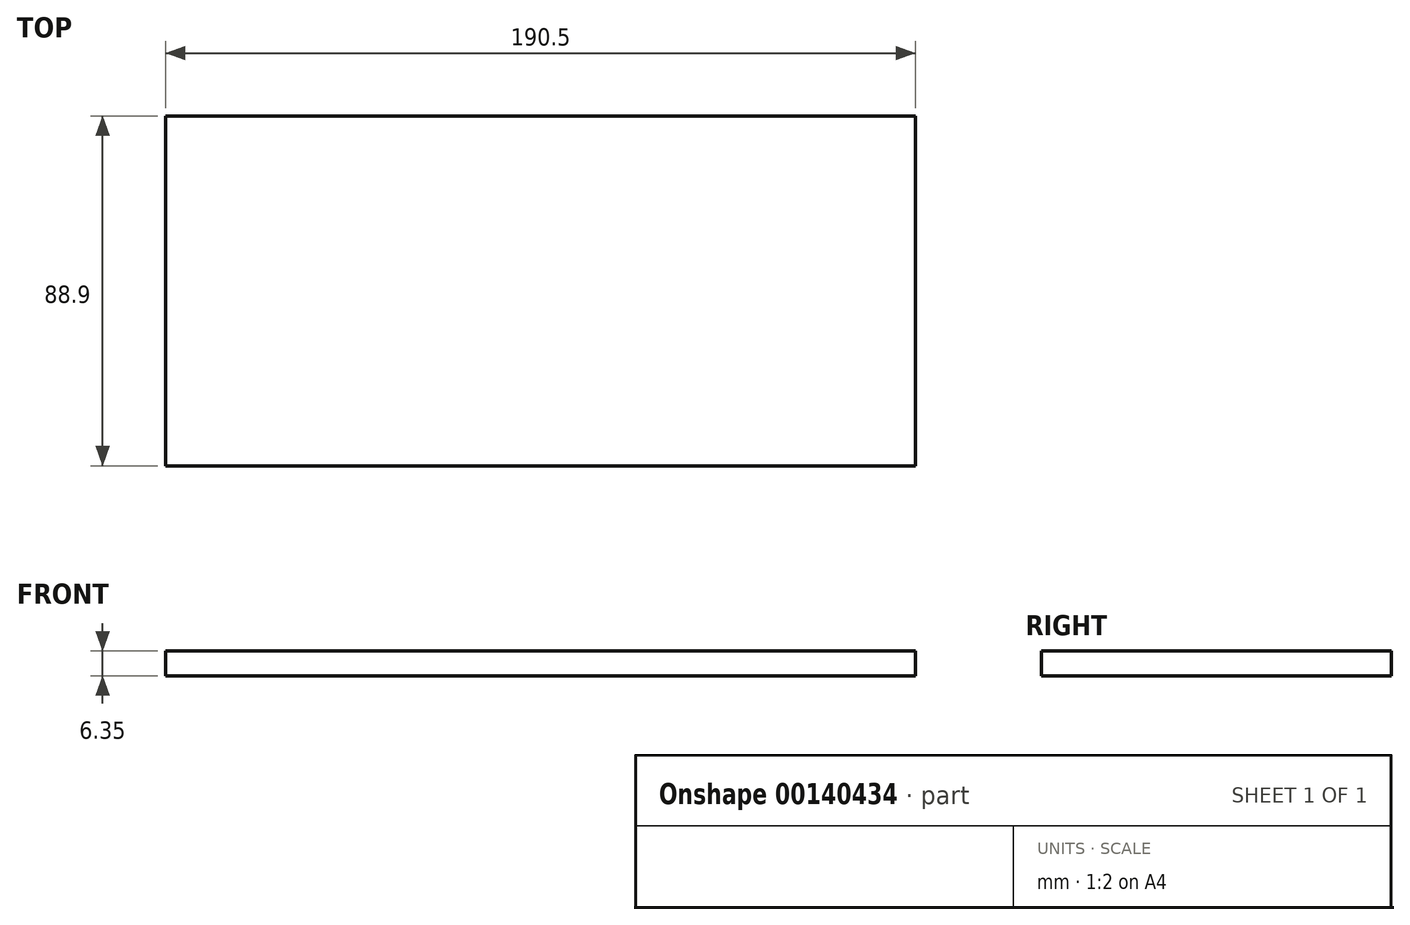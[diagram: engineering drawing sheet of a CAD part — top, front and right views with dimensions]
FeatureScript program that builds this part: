
annotation { "Feature Type Name" : "Feature", "Feature Type Description" : "" }
export const myFeature = defineFeature(function(context is Context, id is Id, definition is map)
    precondition{}
    {
        {
            var Q0;
            Q0=qCreatedBy(makeId("Top.planeOp"),FACE);
            var sketch = newSketch(context, id + "F0", { "sketchPlane" : qUnion([Q0])});
            skLineSegment(sketch, "E0.bottom", {"start": v(95.25, 44.45) * mm, "end": v(-95.25, 44.45) * mm});
            skLineSegment(sketch, "E0.top", {"start": v(95.25, -44.45) * mm, "end": v(-95.25, -44.45) * mm});
            skLineSegment(sketch, "E0.left", {"start": v(95.25, 44.45) * mm, "end": v(95.25, -44.45) * mm});
            skLineSegment(sketch, "E0.right", {"start": v(-95.25, 44.45) * mm, "end": v(-95.25, -44.45) * mm});
            skPoint(sketch, "E0.middle", {"position": v(0, 0) * mm});
            skSolve(sketch);
        }
        {
            var Q0;
            Q0 = qSketchRegion(id + "F0", true);
            extrude(context, id + "F1", {"entities" : qUnion([Q0]), "depth" : 6.35 * mm});
        }
    });
